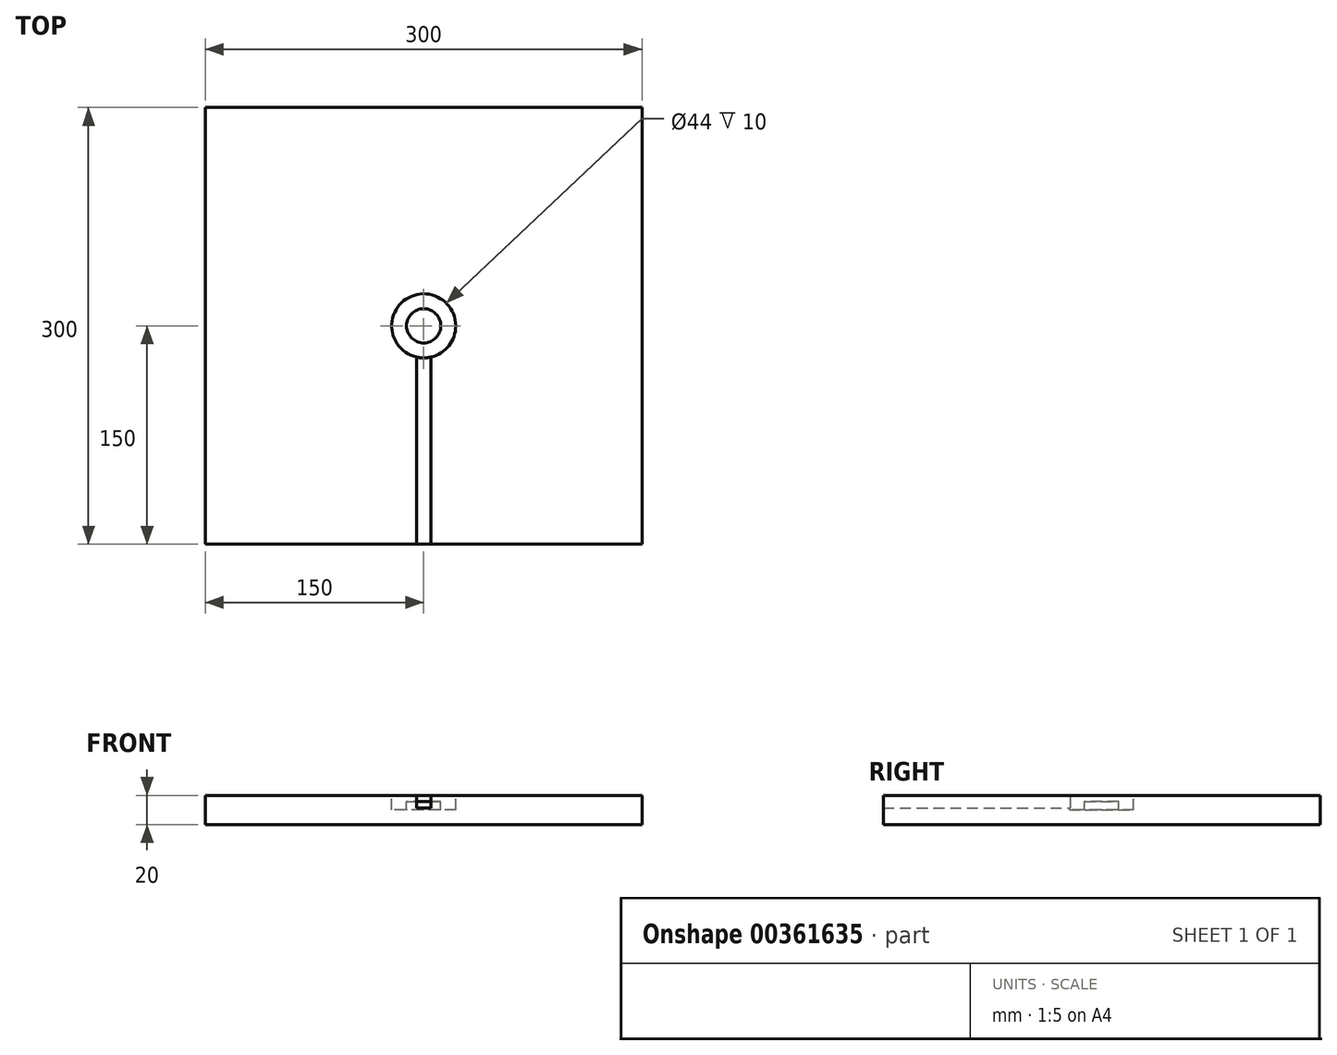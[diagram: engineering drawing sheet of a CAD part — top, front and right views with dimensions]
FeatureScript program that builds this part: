
annotation { "Feature Type Name" : "Feature", "Feature Type Description" : "" }
export const myFeature = defineFeature(function(context is Context, id is Id, definition is map)
    precondition{}
    {
        {
            var Q0;
            Q0=qCreatedBy(makeId("Top.planeOp"),FACE);
            var sketch = newSketch(context, id + "F0", { "sketchPlane" : qUnion([Q0])});
            skLineSegment(sketch, "E0.bottom", {"start": v(150, 150) * mm, "end": v(-150, 150) * mm});
            skLineSegment(sketch, "E0.top", {"start": v(150, -150) * mm, "end": v(-150, -150) * mm});
            skLineSegment(sketch, "E0.left", {"start": v(150, 150) * mm, "end": v(150, -150) * mm});
            skLineSegment(sketch, "E0.right", {"start": v(-150, 150) * mm, "end": v(-150, -150) * mm});
            skPoint(sketch, "E0.middle", {"position": v(0, 0) * mm});
            skSolve(sketch);
        }
        {
            var Q0;
            Q0=qSketchRegion(id+"F0",true);
            extrude(context, id + "F1", {"entities" : qUnion([Q0]), "depth" : 20 * mm});
        }
        {
            var Q0;
            Q0=makeQuery(id+"F1.opExtrude","CAP_FACE",FACE,{"disambiguationData":[OSD([sQuery(id+"F0.wireOp",EDGE,"E0.bottom"),sQuery(id+"F0.wireOp",EDGE,"E0.top"),sQuery(id+"F0.wireOp",EDGE,"E0.left"),sQuery(id+"F0.wireOp",EDGE,"E0.right")])],"isStart":false});
            var sketch = newSketch(context, id + "F2", { "sketchPlane" : qUnion([Q0])});
            skLineSegment(sketch, "E1", {"start": v(-5, -150) * mm, "end": v(-5, -21.42) * mm});
            skLineSegment(sketch, "E2", {"start": v(5, -150) * mm, "end": v(5, -21.42) * mm});
            skArc(sketch, "E3", {"start": v(5, -21.42) * mm, "mid": v(0, 22) * mm, "end": v(-5, -21.42) * mm});
            skCircle(sketch, "E4", {"center": v(0, 0) * mm, "radius": 11.75 * mm});
            skSolve(sketch);
        }
        {
            var Q0;
            {var subQ0=sQuery(id+"F2.wireOp",EDGE,"E3");var subQ1=makeQuery(id+"F2.imprint","INTERSECT",VERTEX,{"derivedFrom":[sQuery(id+"F2.wireOp",EDGE,"E1"),subQ0]});Q0=makeQuery(id+"F2.imprint","IMPRINT",FACE,{"disambiguationData":[TD([[makeQuery(id+"F2.imprint","IMPRINT",EDGE,{"disambiguationData":[TD([[subQ1,-1.0]])],"derivedFrom":subQ0}),1.0]])]});}
            var Q1;
            Q1=sQuery(id+"F2.wireOp",EDGE,"E3");
            extrude(context, id + "F3", {"entities" : qUnion([Q0]), "operationType" : NewBodyOperationType.REMOVE, "surfaceEntities" : qUnion([Q1]), "oppositeDirection" : true, "depth" : 10 * mm});
        }
        {
            var Q0;
            {var subQ0=sQuery(id+"F2.wireOp",EDGE,"E1");Q0=makeQuery(id+"F2.imprint","IMPRINT",FACE,{"disambiguationData":[TD([[makeQuery(id+"F2.imprint","IMPRINT",EDGE,{"derivedFrom":subQ0}),-1.0]])]});}
            extrude(context, id + "F4", {"entities" : qUnion([Q0]), "operationType" : NewBodyOperationType.REMOVE, "oppositeDirection" : true, "depth" : 8.8 * mm});
        }
        {
            var Q0;
            Q0=makeQuery(id+"F3.boolean.opBoolean","COPY",FACE,{"derivedFrom":makeQuery(id+"F3.opExtrude","CAP_FACE",FACE,{"disambiguationData":[OSD([sQuery(id+"F0.wireOp",EDGE,"E0.top"),sQuery(id+"F2.wireOp",EDGE,"E1"),sQuery(id+"F2.wireOp",EDGE,"E2"),sQuery(id+"F2.wireOp",EDGE,"E3")])],"isStart":false})});
            var sketch = newSketch(context, id + "F5", { "sketchPlane" : qUnion([Q0])});
            skArc(sketch, "E5", {"start": v(-5, -21.42) * mm, "mid": v(0, -22) * mm, "end": v(5, -21.42) * mm});
            skSolve(sketch);
        }
        {
            var Q0;
            Q0=makeQuery(id+"F5.imprint","IMPRINT",FACE,{"disambiguationData":[TD([[makeQuery(id+"F5.imprint","IMPRINT",EDGE,{"derivedFrom":sQuery(id+"F5.wireOp",EDGE,"E5")}),-1.0]])]});
            extrude(context, id + "F6", {"entities" : qUnion([Q0]), "operationType" : NewBodyOperationType.ADD, "depth" : 1.2 * mm});
        }
        {
            var Q0;
            Q0 = qSketchRegion(id + "F2", true);
            extrude(context, id + "F7", {"entities" : qUnion([Q0]), "operationType" : NewBodyOperationType.REMOVE, "oppositeDirection" : true, "depth" : 4.2 * mm});
        }
    });
